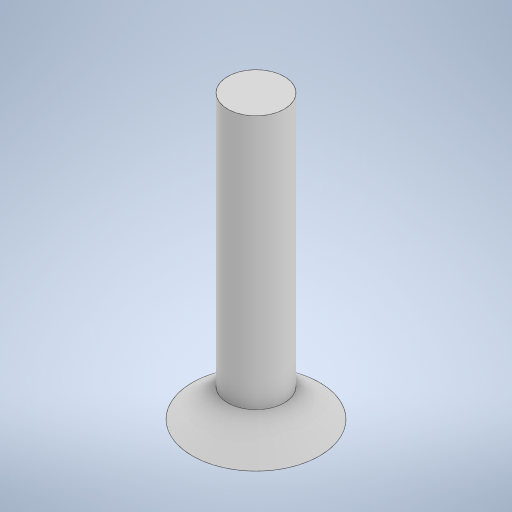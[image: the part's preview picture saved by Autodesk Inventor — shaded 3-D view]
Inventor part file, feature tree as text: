
AUTODESK INVENTOR PART (.ipt)
format: ipt  version: 2024 (Build 280153000, 153)  size: 239,104 bytes
history: native  units: mm
features: extrude x2, sketch x2, chamfer x1, projected_geometry x1
ambient origin geometry x8: Origin, YZ Plane, XZ Plane, XY Plane, X Axis, Y Axis, Z Axis, Center Point
bodies: Solid1 (feature_tree)
feature tree (6):
  extrude  "Extrusion1"  Depth=2.0mm TaperAngle=0.0deg
  chamfer  "Chamfer1"  Distance=2.0mm Angle=45.0deg
  extrude  "Extrusion2"  [1 undecoded]
  sketch  "Sketch1"  dims[d0=9.0mm d1=2.0mm d2=0.0mm d3=2.5mm d4=2.0mm d5=45.0deg]
  sketch  "Sketch2"  dims[d6=18.0mm d7=0.0mm]
  projected_geometry  "Projected Loop1"
note: 1 required parameter value undecoded (feature->parameter linkage not recoverable at this tier; creation-order binding heuristic only, values carry confidence <= 0.55)
